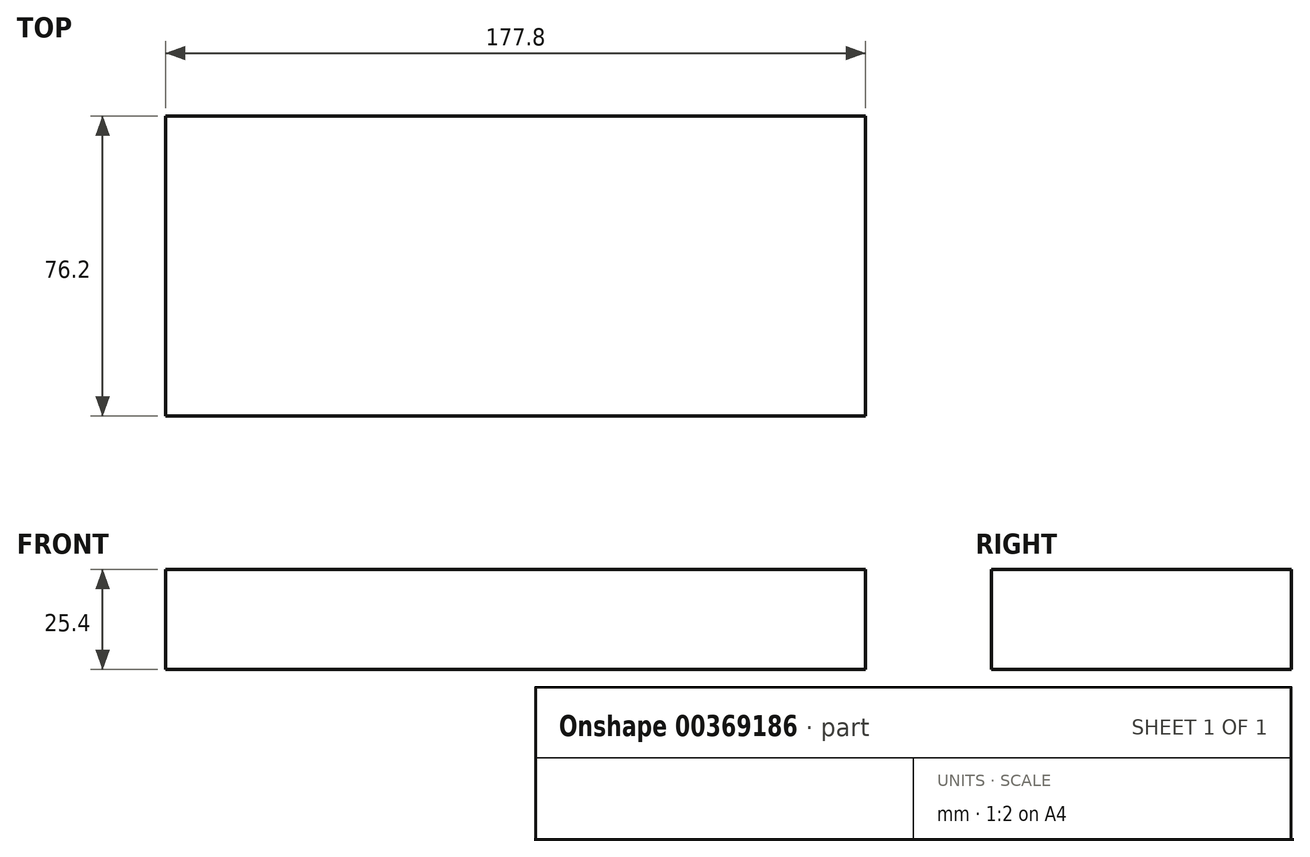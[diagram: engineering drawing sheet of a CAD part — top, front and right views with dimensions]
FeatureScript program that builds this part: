
annotation { "Feature Type Name" : "Feature", "Feature Type Description" : "" }
export const myFeature = defineFeature(function(context is Context, id is Id, definition is map)
    precondition{}
    {
        {
            var Q0;
            Q0=qCreatedBy(makeId("Top.planeOp"),FACE);
            var sketch = newSketch(context, id + "F0", { "sketchPlane" : qUnion([Q0])});
            skLineSegment(sketch, "E0.bottom", {"start": v(-88.9, 38.1) * mm, "end": v(88.9, 38.1) * mm});
            skLineSegment(sketch, "E0.top", {"start": v(-88.9, -38.1) * mm, "end": v(88.9, -38.1) * mm});
            skLineSegment(sketch, "E0.left", {"start": v(-88.9, 38.1) * mm, "end": v(-88.9, -38.1) * mm});
            skLineSegment(sketch, "E0.right", {"start": v(88.9, 38.1) * mm, "end": v(88.9, -38.1) * mm});
            skPoint(sketch, "E0.middle", {"position": v(0, 0) * mm});
            skSolve(sketch);
        }
        {
            var Q0;
            Q0 = qSketchRegion(id + "F0", true);
            extrude(context, id + "F1", {"entities" : qUnion([Q0]), "depth" : 25.4 * mm});
        }
    });
